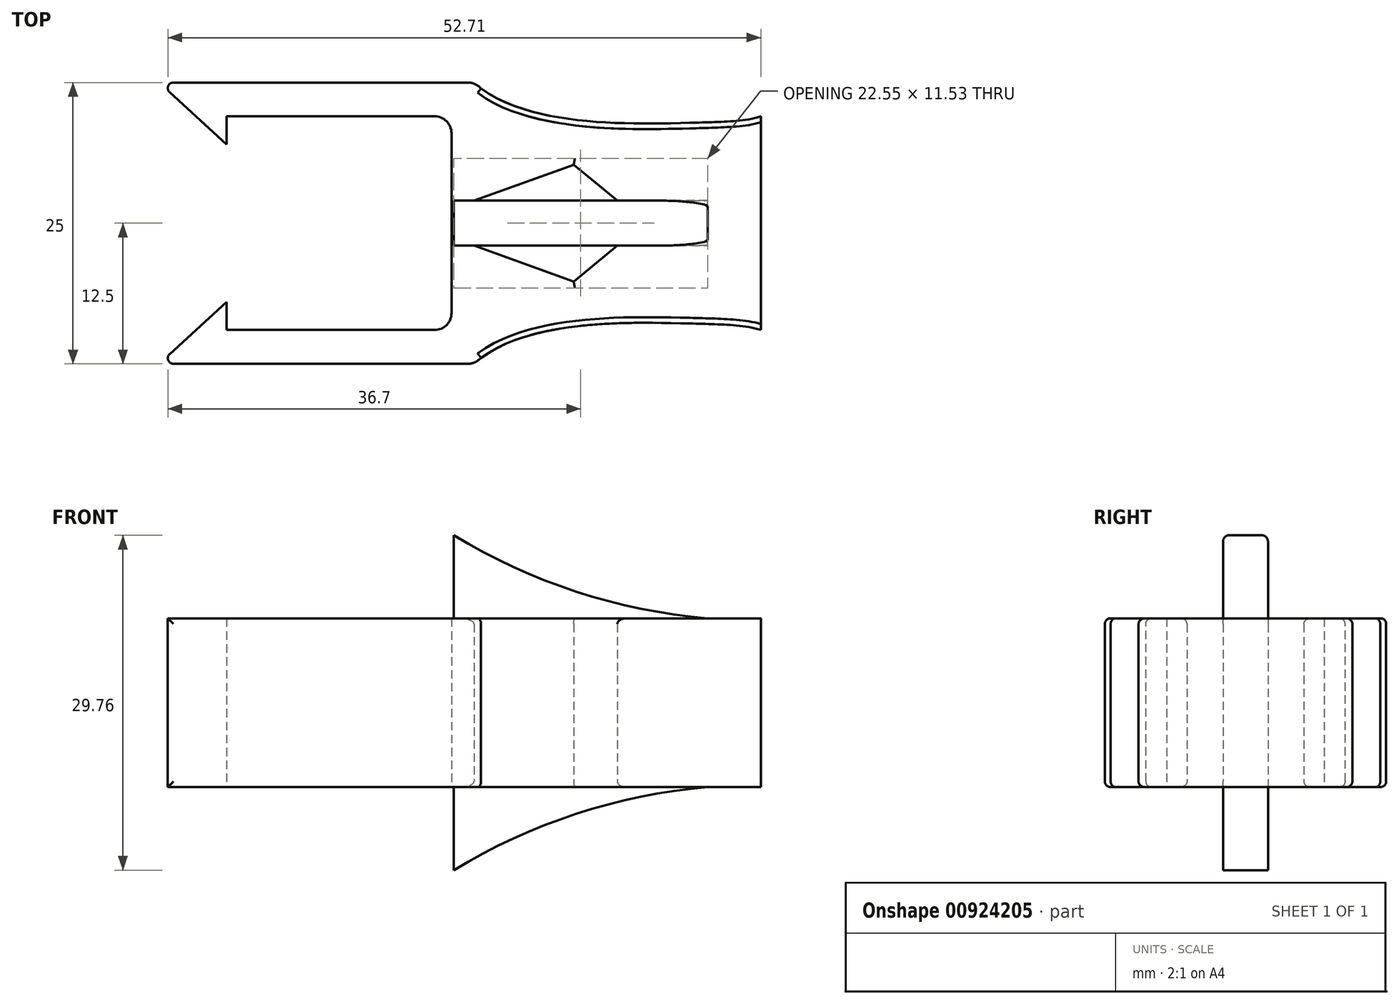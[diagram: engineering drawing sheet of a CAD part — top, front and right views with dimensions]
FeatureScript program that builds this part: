
annotation { "Feature Type Name" : "Feature", "Feature Type Description" : "" }
export const myFeature = defineFeature(function(context is Context, id is Id, definition is map)
    precondition{}
    {
        {
            var Q0;
            Q0=qCreatedBy(makeId("Top.planeOp"),FACE);
            var sketch = newSketch(context, id + "F0", { "sketchPlane" : qUnion([Q0])});
            skLineSegment(sketch, "E0.bottom", {"start": v(10, -9.5) * mm, "end": v(-10, -9.5) * mm});
            skLineSegment(sketch, "E0.top", {"start": v(10, 9.5) * mm, "end": v(-10, 9.5) * mm});
            skLineSegment(sketch, "E0.left", {"start": v(10, -9.5) * mm, "end": v(10, 9.5) * mm});
            skLineSegment(sketch, "E0.right", {"start": v(-10, -9.5) * mm, "end": v(-10, -7) * mm});
            skPoint(sketch, "E0.middle", {"position": v(0, 0) * mm});
            skLineSegment(sketch, "E1.bottom", {"start": v(12, -12.5) * mm, "end": v(-12, -12.5) * mm});
            skLineSegment(sketch, "E1.top", {"start": v(12, 12.5) * mm, "end": v(-12, 12.5) * mm});
            skLineSegment(sketch, "E1.left", {"start": v(12, -12.5) * mm, "end": v(12, 12.5) * mm});
            skLineSegment(sketch, "E2", {"start": v(-12, 12.5) * mm, "end": v(-16, 12.5) * mm});
            skLineSegment(sketch, "E3", {"start": v(-16, 12.5) * mm, "end": v(-10, 7) * mm});
            skLineSegment(sketch, "E4", {"start": v(-10, 7) * mm, "end": v(-10, 9.5) * mm});
            skLineSegment(sketch, "E5.MirrorCS", {"start": v(-16, -12.5) * mm, "end": v(-10, -7) * mm});
            skLineSegment(sketch, "E6.MirrorCS", {"start": v(-10, -7) * mm, "end": v(-10, -11) * mm});
            skLineSegment(sketch, "E7", {"start": v(-12, -12.5) * mm, "end": v(-16, -12.5) * mm});
            skLineSegment(sketch, "E8.left", {"start": v(37.5, 9.5) * mm, "end": v(37.5, -9.5) * mm});
            skFitSpline(sketch, "E9", {"points": [v(12, 12.5) * mm, v(31.18, 8.92) * mm, v(37.5, 9.5) * mm], "startDerivative": vector(20.47, -18.62) * mm, "endDerivative": vector(10.28, 3.68) * mm});
            skFitSpline(sketch, "E10.MirrorCS", {"points": [v(12, -12.5) * mm, v(31.18, -8.92) * mm, v(37.5, -9.5) * mm], "startDerivative": vector(20.47, 18.62) * mm, "endDerivative": vector(10.28, -3.68) * mm});
            skLineSegment(sketch, "E11", {"start": v(37.5, 0) * mm, "end": v(12, 0) * mm});
            skLineSegment(sketch, "E12.0", {"start": v(37.5, 2) * mm, "end": v(12, 2) * mm});
            skLineSegment(sketch, "E13.0", {"start": v(37.5, -2) * mm, "end": v(12, -2) * mm});
            skLineSegment(sketch, "E14", {"start": v(37.5, -9.5) * mm, "end": v(24.75, -2) * mm});
            skLineSegment(sketch, "E15", {"start": v(24.75, -2) * mm, "end": v(12, -12.5) * mm});
            skLineSegment(sketch, "E16", {"start": v(37.5, -2) * mm, "end": v(31.18, -8.92) * mm});
            skLineSegment(sketch, "E17", {"start": v(31.18, -8.92) * mm, "end": v(12, -2) * mm});
            skLineSegment(sketch, "E18", {"start": v(37.5, 9.5) * mm, "end": v(24.75, 2) * mm});
            skLineSegment(sketch, "E19", {"start": v(24.75, 2) * mm, "end": v(12, 12.5) * mm});
            skLineSegment(sketch, "E20", {"start": v(12, 2) * mm, "end": v(31.18, 8.92) * mm});
            skLineSegment(sketch, "E21", {"start": v(37.5, 2) * mm, "end": v(31.18, 8.92) * mm});
            skSolve(sketch);
        }
        {
            var Q0;
            Q0 = qSketchRegion(id + "F0", true);
            extrude(context, id + "F1", {"entities" : qUnion([Q0]), "endBound" : BoundingType.SYMMETRIC, "depth" : 15 * mm, "offsetDistance" : 25 * mm});
        }
        {
            var Q0;
            Q0=qCreatedBy(makeId("Front.planeOp"),FACE);
            var sketch = newSketch(context, id + "F2", { "sketchPlane" : qUnion([Q0])});
            skLineSegment(sketch, "E22", {"start": v(10.21, 7.38) * mm, "end": v(10.21, 14.88) * mm});
            skArc(sketch, "E23", {"start": v(10.21, 14.88) * mm, "mid": v(23.3, 9.2) * mm, "end": v(37.45, 7.3) * mm});
            skLineSegment(sketch, "E24", {"start": v(10.21, 7.38) * mm, "end": v(37.45, 7.3) * mm});
            skArc(sketch, "E25.MirrorCS", {"start": v(10.21, -14.88) * mm, "mid": v(23.3, -9.2) * mm, "end": v(37.45, -7.3) * mm});
            skLineSegment(sketch, "E26.MirrorCS", {"start": v(10.21, -7.38) * mm, "end": v(37.45, -7.3) * mm});
            skLineSegment(sketch, "E27.MirrorCS", {"start": v(10.21, -7.38) * mm, "end": v(10.21, -14.88) * mm});
            skSolve(sketch);
        }
        {
            var Q0;
            Q0 = qSketchRegion(id + "F2", true);
            extrude(context, id + "F3", {"entities" : qUnion([Q0]), "operationType" : NewBodyOperationType.ADD, "endBound" : BoundingType.SYMMETRIC, "depth" : 4 * mm, "offsetDistance" : 25 * mm});
        }
        {
            var Q0;
            Q0=makeQuery(id+"F1.opExtrude","SWEPT_EDGE",EDGE,{"disambiguationData":[OSD([sQuery(id+"F0.wireOp",EDGE,"E0.top"),sQuery(id+"F0.wireOp",EDGE,"E0.left")])]});
            var Q1;
            Q1=makeQuery(id+"F1.opExtrude","SWEPT_EDGE",EDGE,{"disambiguationData":[OSD([sQuery(id+"F0.wireOp",EDGE,"E0.bottom"),sQuery(id+"F0.wireOp",EDGE,"E0.left")])]});
            var Q2;
            Q2=makeQuery(id+"F1.opExtrude","SWEPT_EDGE",EDGE,{"disambiguationData":[OSD([sQuery(id+"F0.wireOp",EDGE,"E1.top"),sQuery(id+"F0.wireOp",EDGE,"E1.left"),sQuery(id+"F0.wireOp",EDGE,"E9"),sQuery(id+"F0.wireOp",EDGE,"E19")])]});
            var Q3;
            Q3=makeQuery(id+"F1.opExtrude","SWEPT_EDGE",EDGE,{"disambiguationData":[OSD([sQuery(id+"F0.wireOp",EDGE,"E1.bottom"),sQuery(id+"F0.wireOp",EDGE,"E1.left"),sQuery(id+"F0.wireOp",EDGE,"E10.MirrorCS"),sQuery(id+"F0.wireOp",EDGE,"E15")])]});
            fillet(context, id + "F4", {"entities" : qUnion([Q0, Q1, Q2, Q3]), "radius" : 1.5 * mm, "tangentPropagation" : true, "allowEdgeOverflow" : false});
        }
        {
            var Q0;
            Q0=makeQuery(id+"F1.opExtrude","SWEPT_EDGE",EDGE,{"disambiguationData":[OSD([sQuery(id+"F0.wireOp",EDGE,"E2"),sQuery(id+"F0.wireOp",EDGE,"E3")])]});
            var Q1;
            Q1=makeQuery(id+"F1.opExtrude","SWEPT_EDGE",EDGE,{"disambiguationData":[OSD([sQuery(id+"F0.wireOp",EDGE,"E5.MirrorCS"),sQuery(id+"F0.wireOp",EDGE,"E7")])]});
            var Q2;
            {var subQ0=sQuery(id+"F2.wireOp",EDGE,"E23");Q2=makeQuery(id+"F3.opExtrude","CAP_EDGE",EDGE,{"disambiguationData":[OSD([subQ0]),TDD([makeQuery(id+"F2.imprint","IMPRINT",EDGE,{"disambiguationData":[TD([[makeQuery(id+"F2.imprint","INTERSECT",VERTEX,{"derivedFrom":[sQuery(id+"F2.wireOp",EDGE,"E22"),subQ0]}),-1.0]])],"derivedFrom":subQ0})])],"isStart":false});}
            var Q3;
            {var subQ0=sQuery(id+"F2.wireOp",EDGE,"E23");Q3=makeQuery(id+"F3.opExtrude","CAP_EDGE",EDGE,{"disambiguationData":[OSD([subQ0]),TDD([makeQuery(id+"F2.imprint","IMPRINT",EDGE,{"disambiguationData":[TD([[makeQuery(id+"F2.imprint","INTERSECT",VERTEX,{"derivedFrom":[sQuery(id+"F2.wireOp",EDGE,"E22"),subQ0]}),-1.0]])],"derivedFrom":subQ0})])],"isStart":true});}
            var Q4;
            {var subQ0=sQuery(id+"F2.wireOp",EDGE,"E25.MirrorCS");Q4=makeQuery(id+"F3.opExtrude","CAP_EDGE",EDGE,{"disambiguationData":[OSD([subQ0]),TDD([makeQuery(id+"F2.imprint","IMPRINT",EDGE,{"disambiguationData":[TD([[makeQuery(id+"F2.imprint","INTERSECT",VERTEX,{"derivedFrom":[subQ0,sQuery(id+"F2.wireOp",EDGE,"E27.MirrorCS")]}),-1.0]])],"derivedFrom":subQ0})])],"isStart":false});}
            var Q5;
            {var subQ0=sQuery(id+"F2.wireOp",EDGE,"E25.MirrorCS");Q5=makeQuery(id+"F3.opExtrude","CAP_EDGE",EDGE,{"disambiguationData":[OSD([subQ0]),TDD([makeQuery(id+"F2.imprint","IMPRINT",EDGE,{"disambiguationData":[TD([[makeQuery(id+"F2.imprint","INTERSECT",VERTEX,{"derivedFrom":[subQ0,sQuery(id+"F2.wireOp",EDGE,"E27.MirrorCS")]}),-1.0]])],"derivedFrom":subQ0})])],"isStart":true});}
            var Q6;
            Q6=makeQuery(id+"F1.opExtrude","CAP_EDGE",EDGE,{"disambiguationData":[OSD([sQuery(id+"F0.wireOp",EDGE,"E17")])],"isStart":false});
            var Q7;
            {var subQ0=sQuery(id+"F0.wireOp",EDGE,"E15");Q7=makeQuery(id+"F1.opExtrude","CAP_EDGE",EDGE,{"disambiguationData":[OSD([subQ0]),TDD([makeQuery(id+"F0.imprint","IMPRINT",EDGE,{"disambiguationData":[TD([[makeQuery(id+"F0.imprint","INTERSECT",VERTEX,{"derivedFrom":[subQ0,sQuery(id+"F0.wireOp",EDGE,"E17")]}),1.0]])],"derivedFrom":subQ0})])],"isStart":false});}
            var Q8;
            Q8=makeQuery(id+"F1.opExtrude","CAP_EDGE",EDGE,{"disambiguationData":[OSD([sQuery(id+"F0.wireOp",EDGE,"E20")])],"isStart":false});
            var Q9;
            {var subQ0=sQuery(id+"F0.wireOp",EDGE,"E19");Q9=makeQuery(id+"F1.opExtrude","CAP_EDGE",EDGE,{"disambiguationData":[OSD([subQ0]),TDD([makeQuery(id+"F0.imprint","IMPRINT",EDGE,{"disambiguationData":[TD([[makeQuery(id+"F0.imprint","INTERSECT",VERTEX,{"derivedFrom":[subQ0,sQuery(id+"F0.wireOp",EDGE,"E20")]}),1.0]])],"derivedFrom":subQ0})])],"isStart":false});}
            var Q10;
            Q10=makeQuery(id+"F1.opExtrude","CAP_EDGE",EDGE,{"disambiguationData":[OSD([sQuery(id+"F0.wireOp",EDGE,"E17")])],"isStart":true});
            var Q11;
            {var subQ0=sQuery(id+"F0.wireOp",EDGE,"E15");Q11=makeQuery(id+"F1.opExtrude","CAP_EDGE",EDGE,{"disambiguationData":[OSD([subQ0]),TDD([makeQuery(id+"F0.imprint","IMPRINT",EDGE,{"disambiguationData":[TD([[makeQuery(id+"F0.imprint","INTERSECT",VERTEX,{"derivedFrom":[subQ0,sQuery(id+"F0.wireOp",EDGE,"E17")]}),1.0]])],"derivedFrom":subQ0})])],"isStart":true});}
            var Q12;
            Q12=makeQuery(id+"F1.opExtrude","CAP_EDGE",EDGE,{"disambiguationData":[OSD([sQuery(id+"F0.wireOp",EDGE,"E20")])],"isStart":true});
            var Q13;
            {var subQ0=sQuery(id+"F0.wireOp",EDGE,"E19");Q13=makeQuery(id+"F1.opExtrude","CAP_EDGE",EDGE,{"disambiguationData":[OSD([subQ0]),TDD([makeQuery(id+"F0.imprint","IMPRINT",EDGE,{"disambiguationData":[TD([[makeQuery(id+"F0.imprint","INTERSECT",VERTEX,{"derivedFrom":[subQ0,sQuery(id+"F0.wireOp",EDGE,"E20")]}),1.0]])],"derivedFrom":subQ0})])],"isStart":true});}
            var Q14;
            Q14=makeQuery(id+"F1.opExtrude","CAP_EDGE",EDGE,{"disambiguationData":[OSD([sQuery(id+"F0.wireOp",EDGE,"E9")])],"isStart":false});
            var Q15;
            Q15=makeQuery(id+"F1.opExtrude","CAP_EDGE",EDGE,{"disambiguationData":[OSD([sQuery(id+"F0.wireOp",EDGE,"E9")])],"isStart":true});
            var Q16;
            {var subQ0=sQuery(id+"F0.wireOp",EDGE,"E19");var subQ1=sQuery(id+"F0.wireOp",EDGE,"E9");var subQ2=sQuery(id+"F0.wireOp",EDGE,"E1.top");Q16=makeQuery(id+"F4.opFillet","BLEND_EDGE",EDGE,{"blendedFrom":[makeQuery(id+"F1.opExtrude","SWEPT_EDGE",EDGE,{"disambiguationData":[OSD([subQ2,sQuery(id+"F0.wireOp",EDGE,"E1.left"),subQ1,subQ0])]}),makeQuery(id+"F1.opExtrude","CAP_FACE",FACE,{"disambiguationData":[OSD([sQuery(id+"F0.wireOp",EDGE,"E0.bottom"),sQuery(id+"F0.wireOp",EDGE,"E0.top"),sQuery(id+"F0.wireOp",EDGE,"E0.left"),sQuery(id+"F0.wireOp",EDGE,"E1.bottom"),subQ2,sQuery(id+"F0.wireOp",EDGE,"E2"),sQuery(id+"F0.wireOp",EDGE,"E3"),sQuery(id+"F0.wireOp",EDGE,"E5.MirrorCS"),sQuery(id+"F0.wireOp",EDGE,"E6.MirrorCS"),sQuery(id+"F0.wireOp",EDGE,"E4"),sQuery(id+"F0.wireOp",EDGE,"E7"),sQuery(id+"F0.wireOp",EDGE,"E8.left"),subQ1,sQuery(id+"F0.wireOp",EDGE,"E10.MirrorCS"),sQuery(id+"F0.wireOp",EDGE,"E12.0"),sQuery(id+"F0.wireOp",EDGE,"E13.0"),sQuery(id+"F0.wireOp",EDGE,"E15"),sQuery(id+"F0.wireOp",EDGE,"E17"),subQ0,sQuery(id+"F0.wireOp",EDGE,"E20")])],"isStart":true})],"blendedInto":[makeQuery(id+"F1.opExtrude","CAP_FACE",FACE,{"disambiguationData":[OSD([sQuery(id+"F0.wireOp",EDGE,"E0.bottom"),sQuery(id+"F0.wireOp",EDGE,"E0.top"),sQuery(id+"F0.wireOp",EDGE,"E0.left"),sQuery(id+"F0.wireOp",EDGE,"E1.bottom"),subQ2,sQuery(id+"F0.wireOp",EDGE,"E2"),sQuery(id+"F0.wireOp",EDGE,"E3"),sQuery(id+"F0.wireOp",EDGE,"E5.MirrorCS"),sQuery(id+"F0.wireOp",EDGE,"E6.MirrorCS"),sQuery(id+"F0.wireOp",EDGE,"E4"),sQuery(id+"F0.wireOp",EDGE,"E7"),sQuery(id+"F0.wireOp",EDGE,"E8.left"),subQ1,sQuery(id+"F0.wireOp",EDGE,"E10.MirrorCS"),sQuery(id+"F0.wireOp",EDGE,"E12.0"),sQuery(id+"F0.wireOp",EDGE,"E13.0"),sQuery(id+"F0.wireOp",EDGE,"E15"),sQuery(id+"F0.wireOp",EDGE,"E17"),subQ0,sQuery(id+"F0.wireOp",EDGE,"E20")])],"isStart":true})]});}
            var Q17;
            {var subQ0=sQuery(id+"F0.wireOp",EDGE,"E19");var subQ1=sQuery(id+"F0.wireOp",EDGE,"E9");var subQ2=sQuery(id+"F0.wireOp",EDGE,"E1.top");Q17=makeQuery(id+"F4.opFillet","BLEND_EDGE",EDGE,{"blendedFrom":[makeQuery(id+"F1.opExtrude","SWEPT_EDGE",EDGE,{"disambiguationData":[OSD([subQ2,sQuery(id+"F0.wireOp",EDGE,"E1.left"),subQ1,subQ0])]}),makeQuery(id+"F1.opExtrude","CAP_FACE",FACE,{"disambiguationData":[OSD([sQuery(id+"F0.wireOp",EDGE,"E0.bottom"),sQuery(id+"F0.wireOp",EDGE,"E0.top"),sQuery(id+"F0.wireOp",EDGE,"E0.left"),sQuery(id+"F0.wireOp",EDGE,"E1.bottom"),subQ2,sQuery(id+"F0.wireOp",EDGE,"E2"),sQuery(id+"F0.wireOp",EDGE,"E3"),sQuery(id+"F0.wireOp",EDGE,"E5.MirrorCS"),sQuery(id+"F0.wireOp",EDGE,"E6.MirrorCS"),sQuery(id+"F0.wireOp",EDGE,"E4"),sQuery(id+"F0.wireOp",EDGE,"E7"),sQuery(id+"F0.wireOp",EDGE,"E8.left"),subQ1,sQuery(id+"F0.wireOp",EDGE,"E10.MirrorCS"),sQuery(id+"F0.wireOp",EDGE,"E12.0"),sQuery(id+"F0.wireOp",EDGE,"E13.0"),sQuery(id+"F0.wireOp",EDGE,"E15"),sQuery(id+"F0.wireOp",EDGE,"E17"),subQ0,sQuery(id+"F0.wireOp",EDGE,"E20")])],"isStart":false})],"blendedInto":[makeQuery(id+"F1.opExtrude","CAP_FACE",FACE,{"disambiguationData":[OSD([sQuery(id+"F0.wireOp",EDGE,"E0.bottom"),sQuery(id+"F0.wireOp",EDGE,"E0.top"),sQuery(id+"F0.wireOp",EDGE,"E0.left"),sQuery(id+"F0.wireOp",EDGE,"E1.bottom"),subQ2,sQuery(id+"F0.wireOp",EDGE,"E2"),sQuery(id+"F0.wireOp",EDGE,"E3"),sQuery(id+"F0.wireOp",EDGE,"E5.MirrorCS"),sQuery(id+"F0.wireOp",EDGE,"E6.MirrorCS"),sQuery(id+"F0.wireOp",EDGE,"E4"),sQuery(id+"F0.wireOp",EDGE,"E7"),sQuery(id+"F0.wireOp",EDGE,"E8.left"),subQ1,sQuery(id+"F0.wireOp",EDGE,"E10.MirrorCS"),sQuery(id+"F0.wireOp",EDGE,"E12.0"),sQuery(id+"F0.wireOp",EDGE,"E13.0"),sQuery(id+"F0.wireOp",EDGE,"E15"),sQuery(id+"F0.wireOp",EDGE,"E17"),subQ0,sQuery(id+"F0.wireOp",EDGE,"E20")])],"isStart":false})]});}
            var Q18;
            Q18=makeQuery(id+"F1.opExtrude","CAP_EDGE",EDGE,{"disambiguationData":[OSD([sQuery(id+"F0.wireOp",EDGE,"E1.bottom"),sQuery(id+"F0.wireOp",EDGE,"E7")])],"isStart":false});
            var Q19;
            Q19=makeQuery(id+"F1.opExtrude","CAP_EDGE",EDGE,{"disambiguationData":[OSD([sQuery(id+"F0.wireOp",EDGE,"E1.bottom"),sQuery(id+"F0.wireOp",EDGE,"E7")])],"isStart":true});
            fillet(context, id + "F5", {"entities" : qUnion([Q0, Q1, Q2, Q3, Q4, Q5, Q6, Q7, Q8, Q9, Q10, Q11, Q12, Q13, Q14, Q15, Q16, Q17, Q18, Q19]), "radius" : .5 * mm, "tangentPropagation" : true, "allowEdgeOverflow" : false});
        }
    });
